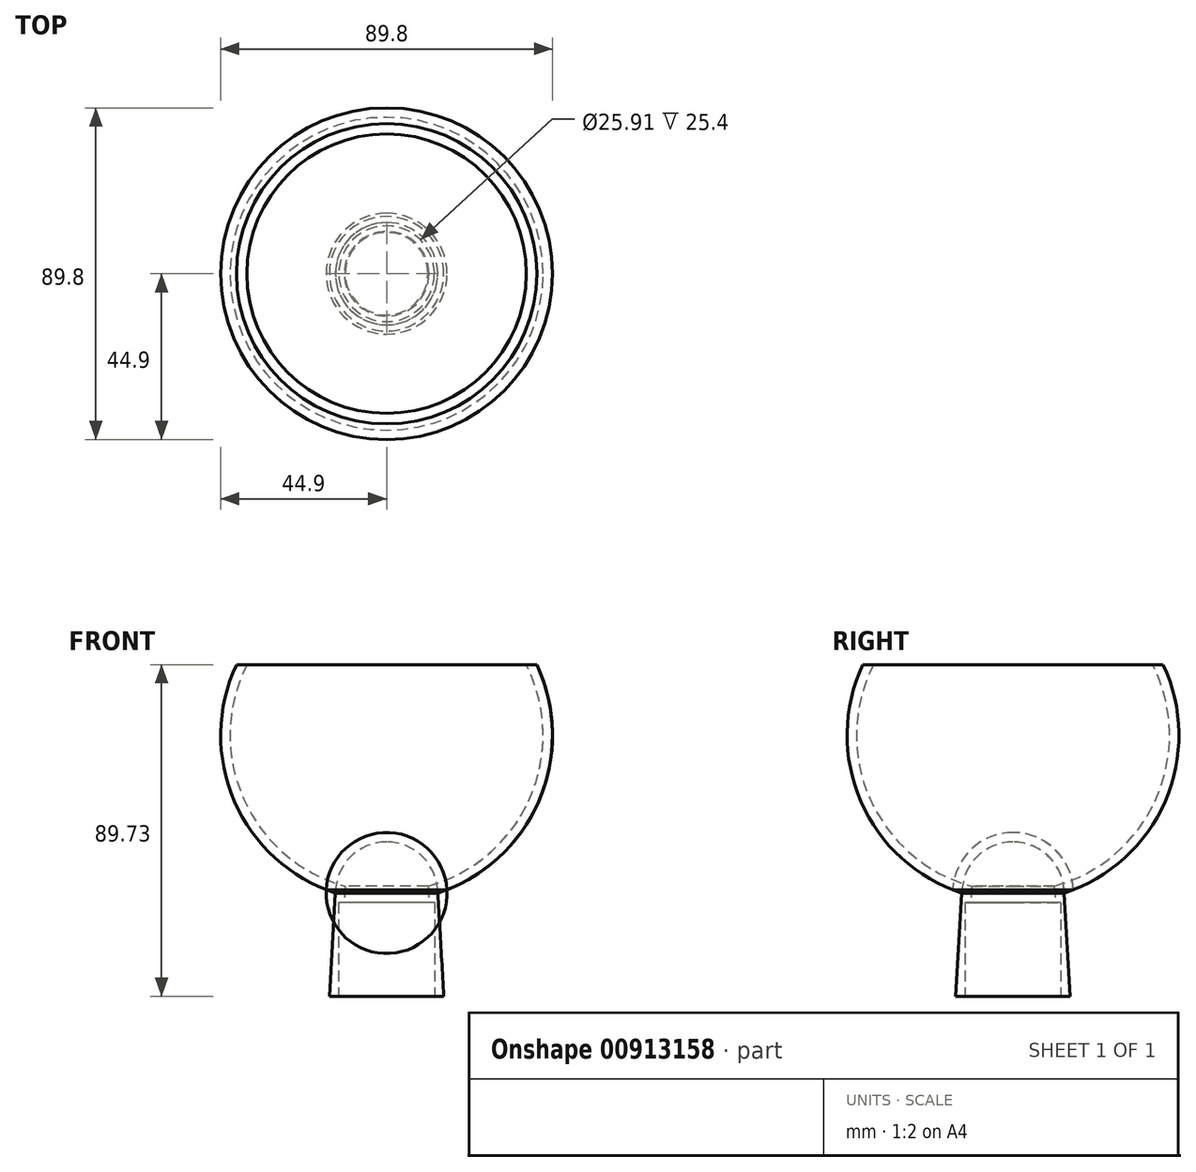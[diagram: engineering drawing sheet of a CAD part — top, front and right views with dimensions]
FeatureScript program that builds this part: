
annotation { "Feature Type Name" : "Feature", "Feature Type Description" : "" }
export const myFeature = defineFeature(function(context is Context, id is Id, definition is map)
    precondition{}
    {
        {
            var Q0;
            Q0=qCreatedBy(makeId("Right.planeOp"),FACE);
            var sketch = newSketch(context, id + "F0", { "sketchPlane" : qUnion([Q0])});
            skLineSegment(sketch, "E0", {"start": v(0, 0) * mm, "end": v(15.5, 0) * mm});
            skLineSegment(sketch, "E1", {"start": v(12.95, 10.05) * mm, "end": v(12.95, 10.05) * mm});
            skLineSegment(sketch, "E2", {"start": v(15.5, 0) * mm, "end": v(13.84, 27.94) * mm});
            skLineSegment(sketch, "E3", {"start": v(0, 89.73) * mm, "end": v(40.64, 89.73) * mm});
            skArc(sketch, "E4", {"start": v(13.84, 27.94) * mm, "mid": v(41.2, 52.79) * mm, "end": v(40.64, 89.73) * mm});
            skLineSegment(sketch, "E5", {"start": v(0, 89.73) * mm, "end": v(0, 0) * mm});
            skArc(sketch, "E6", {"start": v(13.84, 27.94) * mm, "mid": v(9.79, 37.73) * mm, "end": v(0, 41.78) * mm});
            skArc(sketch, "E7", {"start": v(16.36, 28.84) * mm, "mid": v(11.26, 39.84) * mm, "end": v(0, 44.32) * mm});
            skArc(sketch, "E8", {"start": v(16.06, 31.18) * mm, "mid": v(39.88, 55.64) * mm, "end": v(38.1, 89.73) * mm});
            skLineSegment(sketch, "E9", {"start": v(0, 89.73) * mm, "end": v(38.1, 89.73) * mm});
            skLineSegment(sketch, "E10", {"start": v(0, 0) * mm, "end": v(12.95, 0) * mm});
            skLineSegment(sketch, "E11", {"start": v(12.95, 0) * mm, "end": v(11.28, 28.2) * mm});
            skArc(sketch, "E12", {"start": v(13.44, 31.26) * mm, "mid": v(11.83, 30.1) * mm, "end": v(11.28, 28.2) * mm});
            skSolve(sketch);
        }
        {
            var Q0;
            Q0 = qSketchRegion(id + "F0", true);
            var Q1;
            Q1=sQuery(id+"F0.wireOp",EDGE,"E5");
            revolve(context, id + "F1", {"surfaceOperationType" : NewSurfaceOperationType.NEW, "entities" : qUnion([Q0]), "axis" : qUnion([Q1]), "revolveType" : RevolveType.FULL});
        }
        {
            var Q0;
            Q0=makeQuery(id+"F1.opRevolve","SWEPT_FACE",FACE,{"disambiguationData":[OSD([sQuery(id+"F0.wireOp",EDGE,"E3")])]});
            shell(context, id + "F2", {"entities" : qUnion([Q0]), "thickness" : 2.54 * mm});
        }
        {
            var Q0;
            Q0=qCreatedBy(makeId("Top.planeOp"),FACE);
            var sketch = newSketch(context, id + "F3", { "sketchPlane" : qUnion([Q0])});
            skCircle(sketch, "E13", {"center": v(0, 0) * mm, "radius": 12.95 * mm});
            skSolve(sketch);
        }
        {
            var Q0;
            Q0=makeQuery(id+"F3.imprint","IMPRINT",FACE,{"disambiguationData":[TD([[makeQuery(id+"F3.imprint","IMPRINT",EDGE,{"derivedFrom":sQuery(id+"F3.wireOp",EDGE,"E13")}),1.0]])]});
            extrude(context, id + "F4", {"entities" : qUnion([Q0]), "operationType" : NewBodyOperationType.REMOVE, "depth" : 25.4 * mm, "offsetDistance" : 25.4 * mm});
        }
        {
            var Q0;
            {var subQ0=sQuery(id+"F0.wireOp",EDGE,"E6");Q0=makeQuery(id+"F0.imprint","IMPRINT",FACE,{"disambiguationData":[TD([[makeQuery(id+"F0.imprint","IMPRINT",EDGE,{"derivedFrom":subQ0}),-1.0]])]});}
            var Q1;
            Q1=sQuery(id+"F0.wireOp",EDGE,"E5");
            revolve(context, id + "F5", {"surfaceOperationType" : NewSurfaceOperationType.NEW, "entities" : qUnion([Q0]), "axis" : qUnion([Q1]), "revolveType" : RevolveType.FULL});
        }
    });
